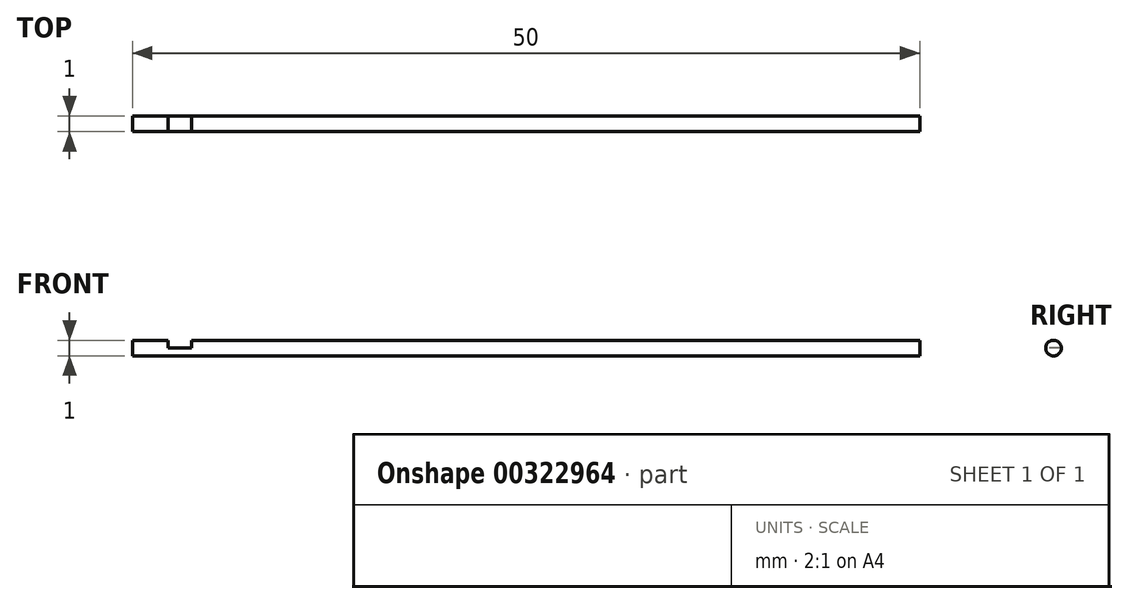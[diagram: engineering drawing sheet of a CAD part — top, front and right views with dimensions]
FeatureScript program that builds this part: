
annotation { "Feature Type Name" : "Feature", "Feature Type Description" : "" }
export const myFeature = defineFeature(function(context is Context, id is Id, definition is map)
    precondition{}
    {
        {
            var Q0;
            Q0=qCreatedBy(makeId("Front.planeOp"),FACE);
            var sketch = newSketch(context, id + "F0", { "sketchPlane" : qUnion([Q0])});
            skLineSegment(sketch, "E0", {"start": v(0, 0) * mm, "end": v(50, 0) * mm});
            skLineSegment(sketch, "E1", {"start": v(50, 0) * mm, "end": v(50, 0.5) * mm});
            skLineSegment(sketch, "E2", {"start": v(50, 0.5) * mm, "end": v(0, 0.5) * mm});
            skLineSegment(sketch, "E3", {"start": v(0, 0.5) * mm, "end": v(0, 0) * mm});
            skSolve(sketch);
        }
        {
            var Q0;
            Q0 = qSketchRegion(id + "F0", true);
            var Q1;
            Q1=sQuery(id+"F0.wireOp",EDGE,"E0");
            revolve(context, id + "F1", {"entities" : qUnion([Q0]), "axis" : qUnion([Q1]), "revolveType" : RevolveType.FULL});
        }
        {
            var Q0;
            Q0=qCreatedBy(makeId("Front.planeOp"),FACE);
            var sketch = newSketch(context, id + "F2", { "sketchPlane" : qUnion([Q0])});
            skLineSegment(sketch, "E4", {"start": v(0, 0) * mm, "end": v(3, 0) * mm, "construction": true});
            skLineSegment(sketch, "E5", {"start": v(3, 0) * mm, "end": v(3, 0.5) * mm, "construction": true});
            skLineSegment(sketch, "E6.bottom", {"start": v(2.25, 0) * mm, "end": v(3.75, 0) * mm});
            skLineSegment(sketch, "E6.top", {"start": v(2.25, 1) * mm, "end": v(3.75, 1) * mm});
            skLineSegment(sketch, "E6.left", {"start": v(2.25, 0) * mm, "end": v(2.25, 1) * mm});
            skLineSegment(sketch, "E6.right", {"start": v(3.75, 0) * mm, "end": v(3.75, 1) * mm});
            skPoint(sketch, "E6.middle", {"position": v(3, 0.5) * mm});
            skSolve(sketch);
        }
        {
            var Q0;
            Q0 = qSketchRegion(id + "F2", true);
            extrude(context, id + "F3", {"entities" : qUnion([Q0]), "operationType" : NewBodyOperationType.REMOVE, "oppositeDirection" : true, "depth" : 25 * mm, "symmetric" : true});
        }
    });
